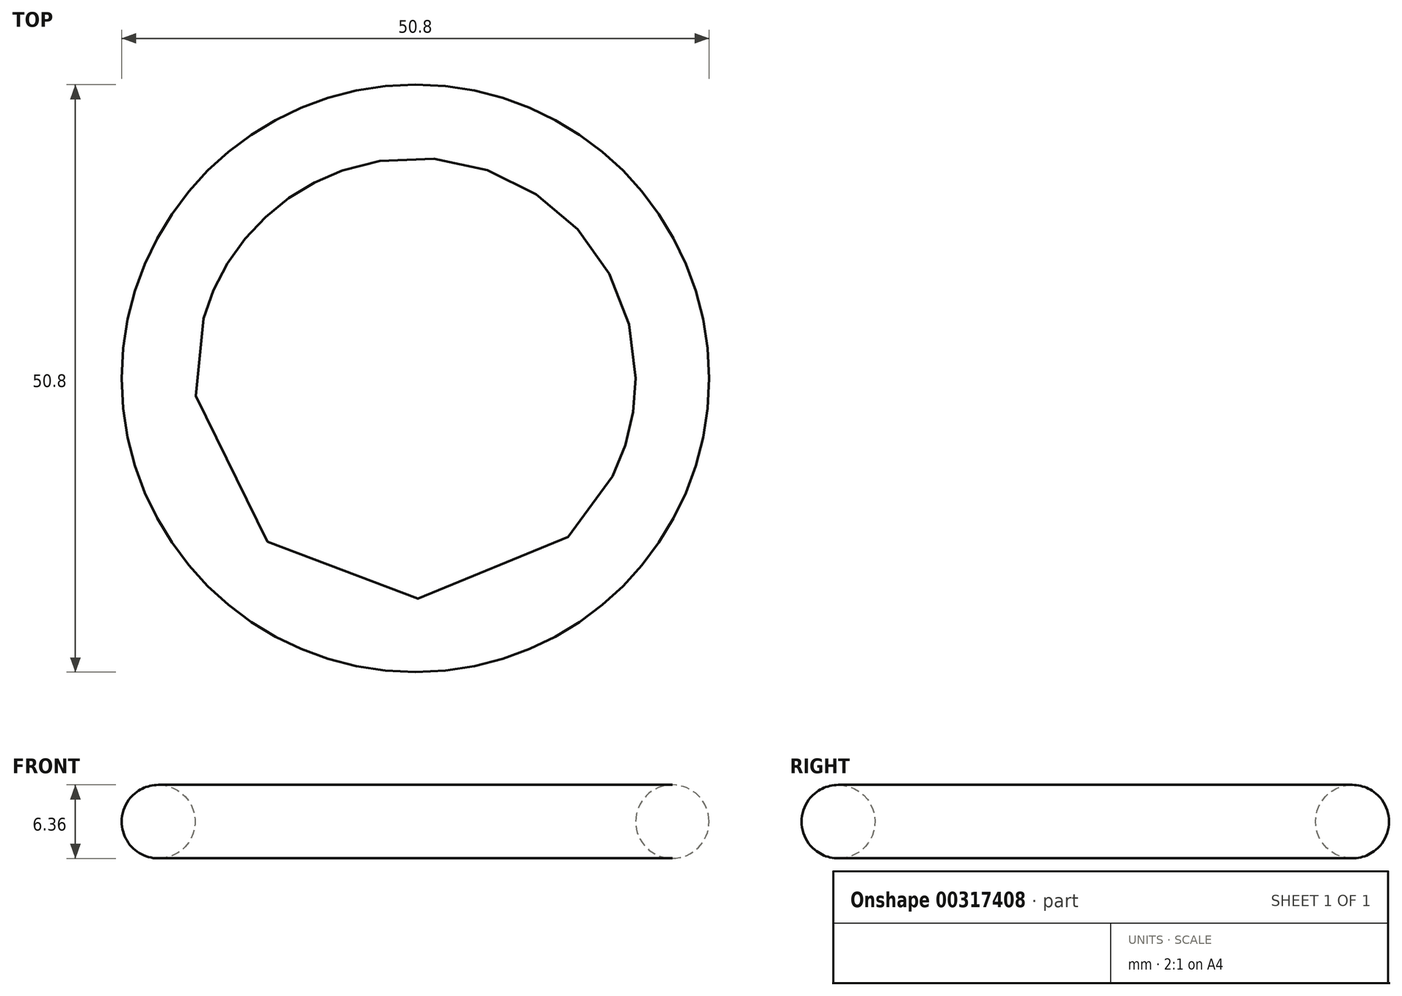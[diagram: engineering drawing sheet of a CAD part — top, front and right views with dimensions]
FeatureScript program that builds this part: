
annotation { "Feature Type Name" : "Feature", "Feature Type Description" : "" }
export const myFeature = defineFeature(function(context is Context, id is Id, definition is map)
    precondition{}
    {
        {
            var Q0;
            Q0=qCreatedBy(makeId("Front.planeOp"),FACE);
            var sketch = newSketch(context, id + "F0", { "sketchPlane" : qUnion([Q0])});
            skCircle(sketch, "E0", {"center": v(-22.23, 0) * mm, "radius": 3.18 * mm});
            skLineSegment(sketch, "E1", {"start": v(0, 12.54) * mm, "end": v(0, -8.2) * mm, "construction": true});
            skSolve(sketch);
        }
        {
            var Q0;
            Q0 = qSketchRegion(id + "F0", true);
            var Q1;
            Q1=sQuery(id+"F0.wireOp",EDGE,"E1");
            revolve(context, id + "F1", {"entities" : qUnion([Q0]), "axis" : qUnion([Q1]), "revolveType" : RevolveType.FULL});
        }
    });
